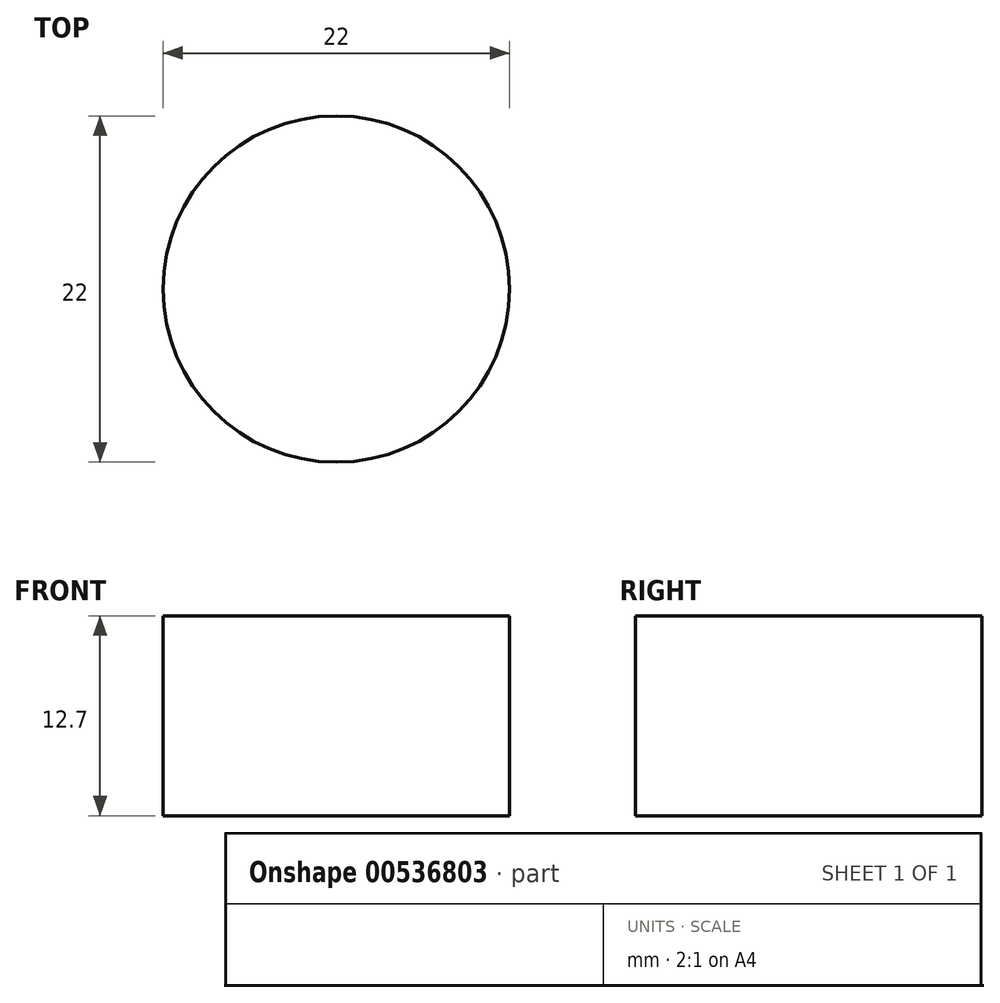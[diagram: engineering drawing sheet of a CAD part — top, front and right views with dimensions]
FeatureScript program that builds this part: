
annotation { "Feature Type Name" : "Feature", "Feature Type Description" : "" }
export const myFeature = defineFeature(function(context is Context, id is Id, definition is map)
    precondition{}
    {
        {
            var Q0;
            Q0=qCreatedBy(makeId("Top.planeOp"),FACE);
            var sketch = newSketch(context, id + "F0", { "sketchPlane" : qUnion([Q0])});
            skCircle(sketch, "E0", {"center": v(0, 0) * mm, "radius": 11 * mm});
            skSolve(sketch);
        }
        {
            assignVariable(context, id + "F1", {"name" : "h", "anyValue" : 12.7 * mm});
        }
        {
            var Q0;
            Q0=makeQuery(id+"F0.imprint","IMPRINT",FACE,{"disambiguationData":[TD([[makeQuery(id+"F0.imprint","IMPRINT",EDGE,{"derivedFrom":sQuery(id+"F0.wireOp",EDGE,"E0")}),1.0]])]});
            extrude(context, id + "F2", {"entities" : qUnion([Q0]), "depth" : getVariable(context, 'h'), "offsetDistance" : 25.4 * mm});
        }
    });
